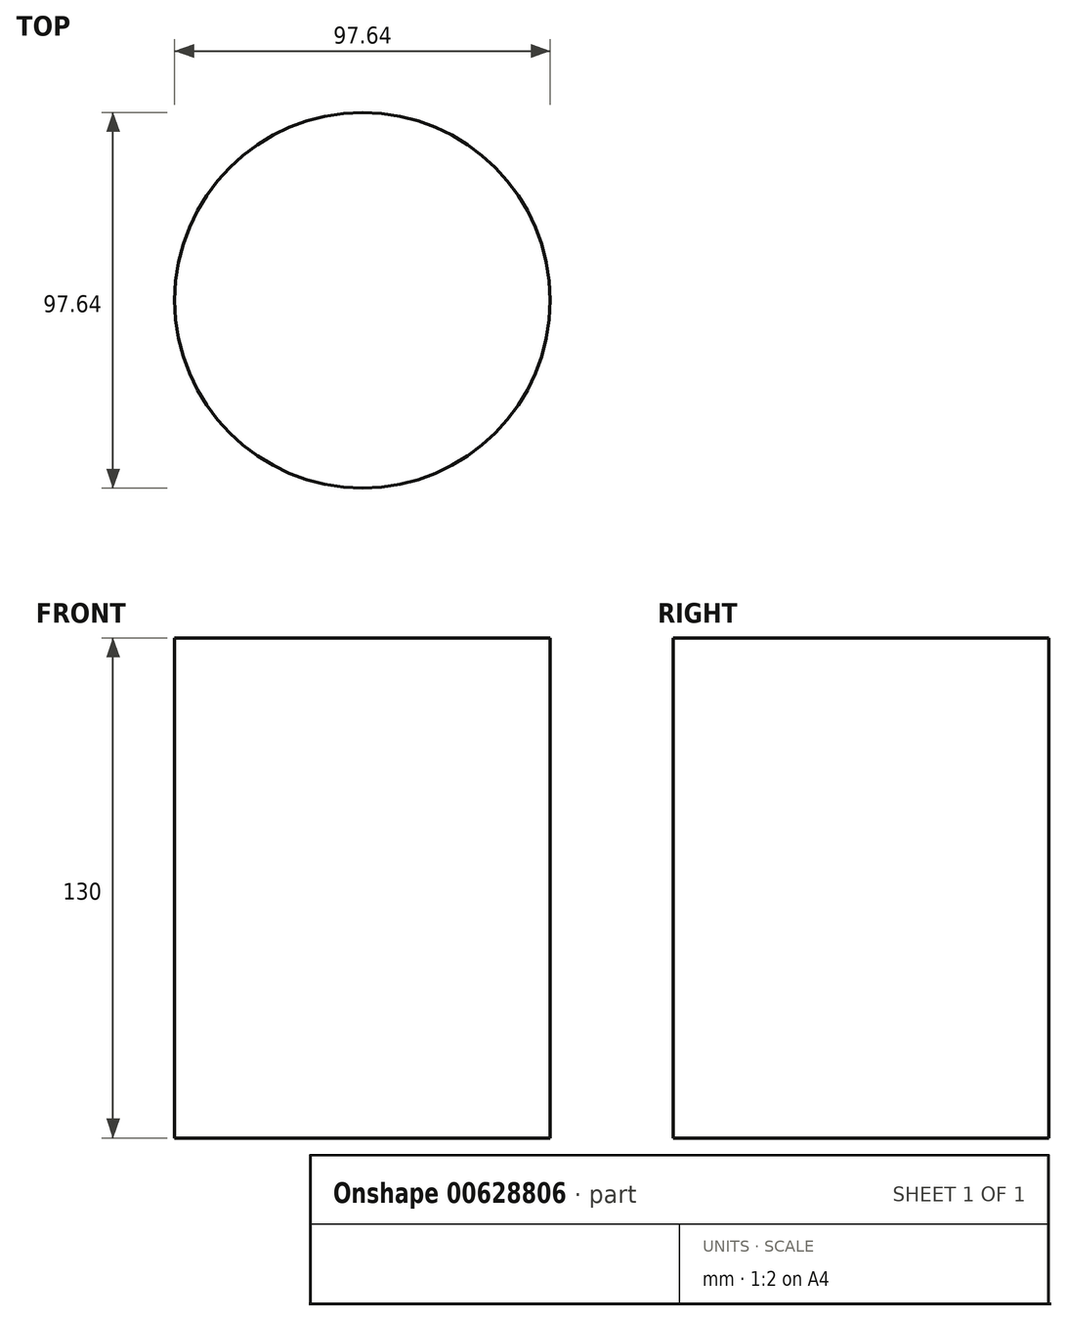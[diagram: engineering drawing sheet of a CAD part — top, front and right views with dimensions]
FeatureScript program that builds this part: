
annotation { "Feature Type Name" : "Feature", "Feature Type Description" : "" }
export const myFeature = defineFeature(function(context is Context, id is Id, definition is map)
    precondition{}
    {
        {
            var Q0;
            Q0=qCreatedBy(makeId("Top.planeOp"),FACE);
            var sketch = newSketch(context, id + "F0", { "sketchPlane" : qUnion([Q0])});
            skCircle(sketch, "E0", {"center": v(0, 0) * mm, "radius": 48.82 * mm});
            skSolve(sketch);
        }
        {
            var Q0;
            Q0=makeQuery(id+"F0.imprint","IMPRINT",FACE,{"disambiguationData":[TD([[makeQuery(id+"F0.imprint","IMPRINT",EDGE,{"derivedFrom":sQuery(id+"F0.wireOp",EDGE,"E0")}),1.0]])]});
            extrude(context, id + "F1", {"entities" : qUnion([Q0]), "depth" : 130 * mm, "offsetDistance" : 25 * mm});
        }
    });
